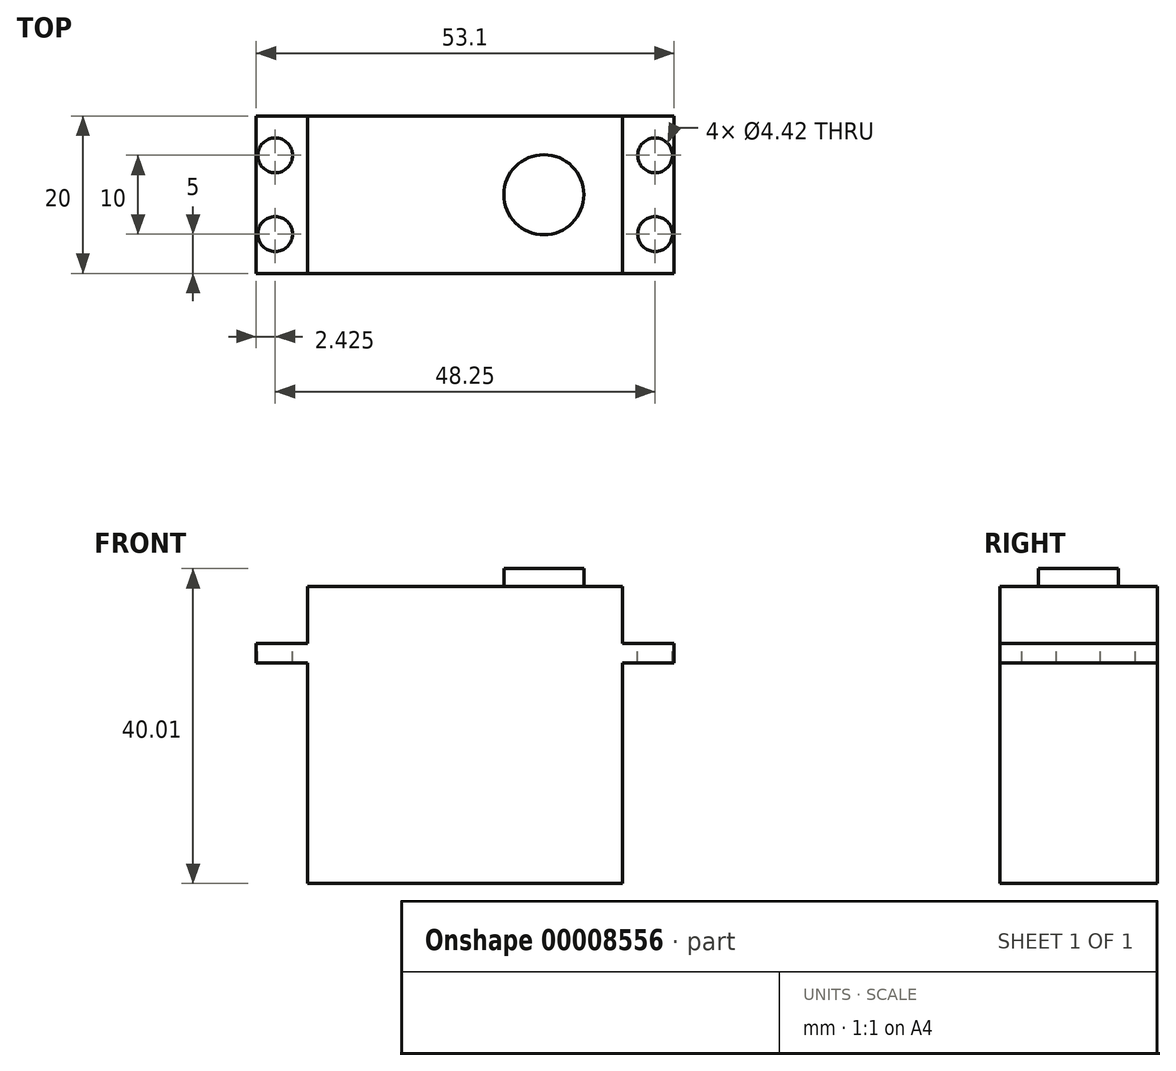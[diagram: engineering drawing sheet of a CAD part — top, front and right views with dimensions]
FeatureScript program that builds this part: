
annotation { "Feature Type Name" : "Feature", "Feature Type Description" : "" }
export const myFeature = defineFeature(function(context is Context, id is Id, definition is map)
    precondition{}
    {
        {
            var Q0;
            Q0=qCreatedBy(makeId("Front.planeOp"),FACE);
            var sketch = newSketch(context, id + "F0", { "sketchPlane" : qUnion([Q0])});
            skLineSegment(sketch, "E0.rect.bottom", {"start": v(20, 18.88) * mm, "end": v(-20, 18.88) * mm});
            skLineSegment(sketch, "E0.rect.top", {"start": v(20, -18.88) * mm, "end": v(-20, -18.88) * mm});
            skLineSegment(sketch, "E0.rect.left", {"start": v(20, 18.88) * mm, "end": v(20, -18.88) * mm});
            skLineSegment(sketch, "E0.rect.right", {"start": v(-20, 18.88) * mm, "end": v(-20, -18.88) * mm});
            skPoint(sketch, "E0.rect.middle", {"position": v(0, 0) * mm});
            skLineSegment(sketch, "E1.bottom", {"start": v(-20, 9.12) * mm, "end": v(-26.55, 9.12) * mm});
            skLineSegment(sketch, "E1.top", {"start": v(-20, 11.62) * mm, "end": v(-26.55, 11.62) * mm});
            skLineSegment(sketch, "E1.left", {"start": v(-20, 9.12) * mm, "end": v(-20, 11.62) * mm});
            skLineSegment(sketch, "E1.right", {"start": v(-26.55, 9.12) * mm, "end": v(-26.55, 11.62) * mm});
            skLineSegment(sketch, "E2.bottom", {"start": v(20, 9.12) * mm, "end": v(26.55, 9.12) * mm});
            skLineSegment(sketch, "E2.top", {"start": v(20, 11.62) * mm, "end": v(26.55, 11.62) * mm});
            skLineSegment(sketch, "E2.left", {"start": v(20, 9.12) * mm, "end": v(20, 11.62) * mm});
            skLineSegment(sketch, "E2.right", {"start": v(26.55, 9.12) * mm, "end": v(26.55, 11.62) * mm});
            skSolve(sketch);
        }
        {
            var Q0;
            Q0 = qSketchRegion(id + "F0", true);
            extrude(context, id + "F1", {"entities" : qUnion([Q0]), "depth" : 20 * mm});
        }
        {
            var Q0;
            Q0=makeQuery(id+"F1.opExtrude","SWEPT_FACE",FACE,{"disambiguationData":[OSD([sQuery(id+"F0.wireOp",EDGE,"E1.top")])]});
            var sketch = newSketch(context, id + "F2", { "sketchPlane" : qUnion([Q0])});
            skLineSegment(sketch, "E3.0.0", {"start": v(-20, 0) * mm, "end": v(-26.55, 0) * mm});
            skLineSegment(sketch, "E3.0.1", {"start": v(-26.55, 0) * mm, "end": v(-26.55, -20) * mm});
            skLineSegment(sketch, "E3.0.2", {"start": v(-26.55, -20) * mm, "end": v(-20, -20) * mm});
            skLineSegment(sketch, "E3.0.3", {"start": v(-20, -20) * mm, "end": v(-20, 0) * mm});
            skLineSegment(sketch, "E4.0.0", {"start": v(26.55, 0) * mm, "end": v(20, 0) * mm});
            skLineSegment(sketch, "E4.0.1", {"start": v(20, 0) * mm, "end": v(20, -20) * mm});
            skLineSegment(sketch, "E4.0.2", {"start": v(20, -20) * mm, "end": v(26.55, -20) * mm});
            skLineSegment(sketch, "E4.0.3", {"start": v(26.55, -20) * mm, "end": v(26.55, 0) * mm});
            skCircle(sketch, "E5", {"center": v(-24.13, -15) * mm, "radius": 2.2 * mm});
            skCircle(sketch, "E6", {"center": v(-24.13, -5) * mm, "radius": 2.2 * mm});
            skCircle(sketch, "E7", {"center": v(24.12, -15) * mm, "radius": 2.2 * mm});
            skCircle(sketch, "E8", {"center": v(24.12, -5) * mm, "radius": 2.2 * mm});
            skLineSegment(sketch, "E9.bottom", {"start": v(-24.13, -15) * mm, "end": v(24.12, -15) * mm, "construction": true});
            skLineSegment(sketch, "E9.top", {"start": v(-24.13, -5) * mm, "end": v(24.12, -5) * mm, "construction": true});
            skLineSegment(sketch, "E9.left", {"start": v(-24.13, -15) * mm, "end": v(-24.13, -5) * mm, "construction": true});
            skLineSegment(sketch, "E9.right", {"start": v(24.12, -15) * mm, "end": v(24.12, -5) * mm, "construction": true});
            skSolve(sketch);
        }
        {
            var Q0;
            Q0=makeQuery(id+"F2.imprint","IMPRINT",FACE,{"disambiguationData":[TD([[makeQuery(id+"F2.imprint","IMPRINT",EDGE,{"derivedFrom":sQuery(id+"F2.wireOp",EDGE,"E6")}),1.0]])]});
            var Q1;
            Q1=makeQuery(id+"F2.imprint","IMPRINT",FACE,{"disambiguationData":[TD([[makeQuery(id+"F2.imprint","IMPRINT",EDGE,{"derivedFrom":sQuery(id+"F2.wireOp",EDGE,"E5")}),1.0]])]});
            var Q2;
            Q2=makeQuery(id+"F2.imprint","IMPRINT",FACE,{"disambiguationData":[TD([[makeQuery(id+"F2.imprint","IMPRINT",EDGE,{"derivedFrom":sQuery(id+"F2.wireOp",EDGE,"E7")}),1.0]])]});
            var Q3;
            Q3=makeQuery(id+"F2.imprint","IMPRINT",FACE,{"disambiguationData":[TD([[makeQuery(id+"F2.imprint","IMPRINT",EDGE,{"derivedFrom":sQuery(id+"F2.wireOp",EDGE,"E8")}),1.0]])]});
            extrude(context, id + "F3", {"entities" : qUnion([Q0, Q1, Q2, Q3]), "operationType" : NewBodyOperationType.REMOVE, "oppositeDirection" : true, "depth" : 25.4 * mm});
        }
        {
            var Q0;
            Q0=makeQuery(id+"F1.opExtrude","SWEPT_FACE",FACE,{"disambiguationData":[OSD([sQuery(id+"F0.wireOp",EDGE,"E0.rect.bottom")])]});
            var sketch = newSketch(context, id + "F4", { "sketchPlane" : qUnion([Q0])});
            skLineSegment(sketch, "E10.0.0", {"start": v(20, 0) * mm, "end": v(-20, 0) * mm});
            skLineSegment(sketch, "E10.0.1", {"start": v(-20, 0) * mm, "end": v(-20, -20) * mm});
            skLineSegment(sketch, "E10.0.2", {"start": v(-20, -20) * mm, "end": v(20, -20) * mm});
            skLineSegment(sketch, "E10.0.3", {"start": v(20, -20) * mm, "end": v(20, 0) * mm});
            skPoint(sketch, "E11", {"position": v(20, -10) * mm});
            skCircle(sketch, "E12", {"center": v(10, -10) * mm, "radius": 5.08 * mm});
            skSolve(sketch);
        }
        {
            var Q0;
            Q0=makeQuery(id+"F4.imprint","IMPRINT",FACE,{"disambiguationData":[TD([[makeQuery(id+"F4.imprint","IMPRINT",EDGE,{"derivedFrom":sQuery(id+"F4.wireOp",EDGE,"E12")}),1.0]])]});
            extrude(context, id + "F5", {"entities" : qUnion([Q0]), "operationType" : NewBodyOperationType.ADD, "depth" : 2.25 * mm});
        }
    });
